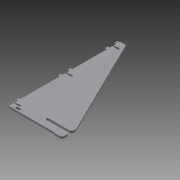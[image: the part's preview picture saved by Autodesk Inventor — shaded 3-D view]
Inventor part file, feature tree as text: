
AUTODESK INVENTOR PART (.ipt)
format: ipt  version: 2015 SP2 (Build 190223200, 223)  size: 218,112 bytes
history: native  units: mm
features: extrude x6, sketch x6, chamfer x2
ambient origin geometry x8: Origin, YZ Plane, XZ Plane, XY Plane, X Axis, Y Axis, Z Axis, Center Point
bodies: Solid1 (feature_tree)
feature tree (14):
  extrude  "Extrusion1"  Depth=183.9mm
  extrude  "Extrusion2"  Depth=47.0mm
  extrude  "Extrusion3"  Depth=9.0mm
  extrude  "Extrusion4"  Depth=9.0mm
  extrude  "Extrusion5"  Depth=6.0mm
  extrude  "Extrusion6"  Depth=6.0mm TaperAngle=0.0deg
  chamfer  "Chamfer1"  Distance=5.1mm
  chamfer  "Chamfer2"  Distance=4.4mm
  sketch  "Sketch1"  dims[d0=370.0mm d1=183.9mm]
  sketch  "Sketch2"  dims[d2=25.4mm d3=47.0mm]
  sketch  "Sketch3"  dims[d4=6.0mm d5=0.0mm d6=9.0mm]
  sketch  "Sketch4"  dims[d7=9.0mm d8=9.0mm]
  sketch  "Sketch5"  dims[d9=9.0mm d12=6.0mm]
  sketch  "Sketch6"  dims[d14=9.0mm d18=6.0mm d19=0.0mm d20=5.1mm d21=4.4mm d22=17.1mm d23=21.1mm d25=8.0mm d28=6.0mm d29=0.0mm d32=6.0mm d33=0.0mm d34=8.8mm d35=2.0mm d36=150.8mm d37=28.0mm d38=75.0mm d39=6.0mm d40=0.0mm d41=8.0mm d42=8.0mm d43=8.0mm d44=24.0mm d45=6.0mm d46=0.0mm d47=2.0mm d48=2.0mm d49=45.0deg d50=5.0mm d51=2.0mm d52=45.0deg d53=32.15mm d54=171.35mm d55=203.65mm d56=326.443mm d57=358.743mm d58=192.0mm d59=20.51mm d60=347.093mm]
